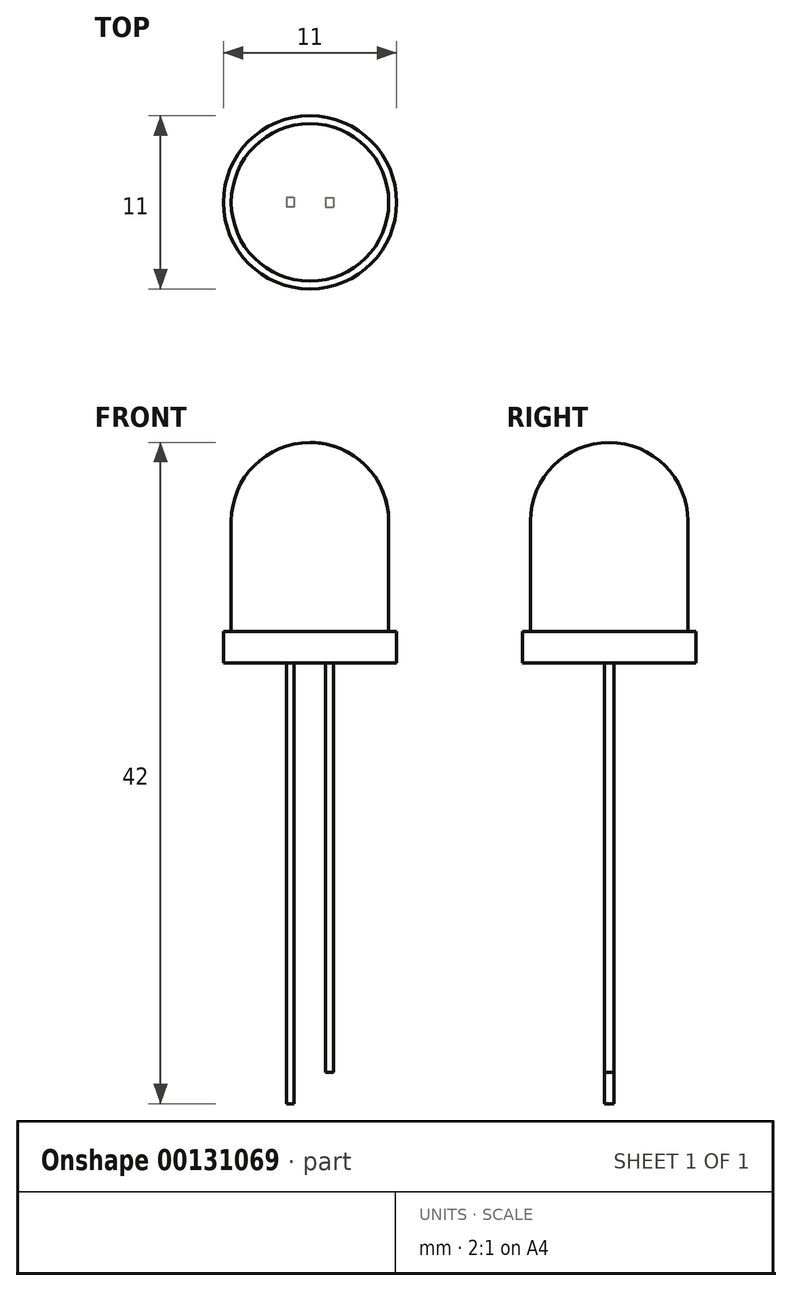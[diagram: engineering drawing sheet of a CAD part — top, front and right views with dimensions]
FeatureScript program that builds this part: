
annotation { "Feature Type Name" : "Feature", "Feature Type Description" : "" }
export const myFeature = defineFeature(function(context is Context, id is Id, definition is map)
    precondition{}
    {
        {
            var Q0;
            Q0=qCreatedBy(makeId("Top.planeOp"),FACE);
            var sketch = newSketch(context, id + "F0", { "sketchPlane" : qUnion([Q0])});
            skCircle(sketch, "E0", {"center": v(0, 0) * mm, "radius": 5 * mm});
            skSolve(sketch);
        }
        {
            var Q0;
            Q0 = qSketchRegion(id + "F0", true);
            extrude(context, id + "F1", {"entities" : qUnion([Q0]), "depth" : 7 * mm, "offsetDistance" : 25.4 * mm});
        }
        {
            var Q0;
            Q0=qCreatedBy(makeId("Front.planeOp"),FACE);
            var sketch = newSketch(context, id + "F2", { "sketchPlane" : qUnion([Q0])});
            skLineSegment(sketch, "E1.0", {"start": v(-5, 7) * mm, "end": v(5, 7) * mm});
            skArc(sketch, "E2", {"start": v(5, 7) * mm, "mid": v(0, 12) * mm, "end": v(-5, 7) * mm});
            skLineSegment(sketch, "E3", {"start": v(0, 14) * mm, "end": v(0, 7) * mm});
            skSolve(sketch);
        }
        {
            var Q0;
            {var subQ0=sQuery(id+"F2.wireOp",EDGE,"E2");var subQ1=sQuery(id+"F2.wireOp",EDGE,"E1.0");var subQ2=makeQuery(id+"F2.imprint","INTERSECT",VERTEX,{"disambiguationData":[OD(1.0)],"derivedFrom":[subQ1,subQ0]});Q0=makeQuery(id+"F2.imprint","IMPRINT",FACE,{"disambiguationData":[TD([[makeQuery(id+"F2.imprint","IMPRINT",EDGE,{"disambiguationData":[TD([[subQ2,1.0]])],"derivedFrom":subQ1}),1.0]])]});}
            var Q1;
            Q1=sQuery(id+"F2.wireOp",EDGE,"E3");
            revolve(context, id + "F3", {"operationType" : NewBodyOperationType.ADD, "surfaceOperationType" : NewSurfaceOperationType.NEW, "entities" : qUnion([Q0]), "axis" : qUnion([Q1]), "revolveType" : RevolveType.FULL});
        }
        {
            var Q0;
            Q0=makeQuery(id+"F1.opExtrude","CAP_FACE",FACE,{"disambiguationData":[OSD([sQuery(id+"F0.wireOp",EDGE,"E0")])],"isStart":true});
            var sketch = newSketch(context, id + "F4", { "sketchPlane" : qUnion([Q0])});
            skCircle(sketch, "E4", {"center": v(0, 0) * mm, "radius": 5.5 * mm});
            skSolve(sketch);
        }
        {
            var Q0;
            Q0=makeQuery(id+"F4.imprint","IMPRINT",FACE,{"disambiguationData":[TD([[makeQuery(id+"F4.imprint","IMPRINT",EDGE,{"derivedFrom":sQuery(id+"F4.wireOp",EDGE,"E4")}),1.0]])]});
            var Q1;
            Q1=makeQuery(id+"F4.imprint","IMPRINT",FACE,{"disambiguationData":[TD([[makeQuery(id+"F4.imprint","IMPRINT",EDGE,{"derivedFrom":makeQuery(id+"F1.opExtrude","CAP_EDGE",EDGE,{"disambiguationData":[OSD([sQuery(id+"F0.wireOp",EDGE,"E0")])],"isStart":true})}),-1.0]])]});
            extrude(context, id + "F5", {"entities" : qUnion([Q0, Q1]), "operationType" : NewBodyOperationType.ADD, "depth" : 2 * mm, "offsetDistance" : 25.4 * mm});
        }
        {
            var Q0;
            Q0=makeQuery(id+"F5.opExtrude","CAP_FACE",FACE,{"disambiguationData":[OSD([sQuery(id+"F4.wireOp",EDGE,"E4")])],"isStart":false});
            var sketch = newSketch(context, id + "F6", { "sketchPlane" : qUnion([Q0])});
            skLineSegment(sketch, "E5", {"start": v(-1.25, 0) * mm, "end": v(1.25, 0) * mm});
            skLineSegment(sketch, "E6.bottom", {"start": v(1, -0.3) * mm, "end": v(1.5, -0.3) * mm});
            skLineSegment(sketch, "E6.top", {"start": v(1, 0.3) * mm, "end": v(1.5, 0.3) * mm});
            skLineSegment(sketch, "E6.left", {"start": v(1, -0.3) * mm, "end": v(1, 0.3) * mm});
            skLineSegment(sketch, "E6.right", {"start": v(1.5, -0.3) * mm, "end": v(1.5, 0.3) * mm});
            skPoint(sketch, "E6.middle", {"position": v(1.25, 0) * mm});
            skLineSegment(sketch, "E7", {"start": v(0, 0) * mm, "end": v(0, -2.7) * mm});
            skLineSegment(sketch, "E8.MirrorCS", {"start": v(-1, -0.3) * mm, "end": v(-1.5, -0.3) * mm});
            skPoint(sketch, "E9.MirrorP", {"position": v(-1.25, 0) * mm});
            skLineSegment(sketch, "E10.MirrorCS", {"start": v(-1.5, -0.3) * mm, "end": v(-1.5, 0.3) * mm});
            skLineSegment(sketch, "E11.MirrorCS", {"start": v(-1, 0.3) * mm, "end": v(-1.5, 0.3) * mm});
            skLineSegment(sketch, "E12.MirrorCS", {"start": v(-1, -0.3) * mm, "end": v(-1, 0.3) * mm});
            skSolve(sketch);
        }
        {
            var Q0;
            {var subQ1=sQuery(id+"F6.wireOp",EDGE,"E8.MirrorCS");Q0=makeQuery(id+"F6.imprint","IMPRINT",FACE,{"disambiguationData":[TD([[makeQuery(id+"F6.imprint","IMPRINT",EDGE,{"derivedFrom":subQ1}),-1.0]])]});}
            extrude(context, id + "F7", {"entities" : qUnion([Q0]), "operationType" : NewBodyOperationType.ADD, "depth" : 28 * mm, "offsetDistance" : 25.4 * mm});
        }
        {
            var Q0;
            {var subQ3=sQuery(id+"F6.wireOp",EDGE,"E6.bottom");Q0=makeQuery(id+"F6.imprint","IMPRINT",FACE,{"disambiguationData":[TD([[makeQuery(id+"F6.imprint","IMPRINT",EDGE,{"derivedFrom":subQ3}),1.0]])]});}
            extrude(context, id + "F8", {"entities" : qUnion([Q0]), "operationType" : NewBodyOperationType.ADD, "depth" : 26 * mm, "offsetDistance" : 25.4 * mm});
        }
    });
